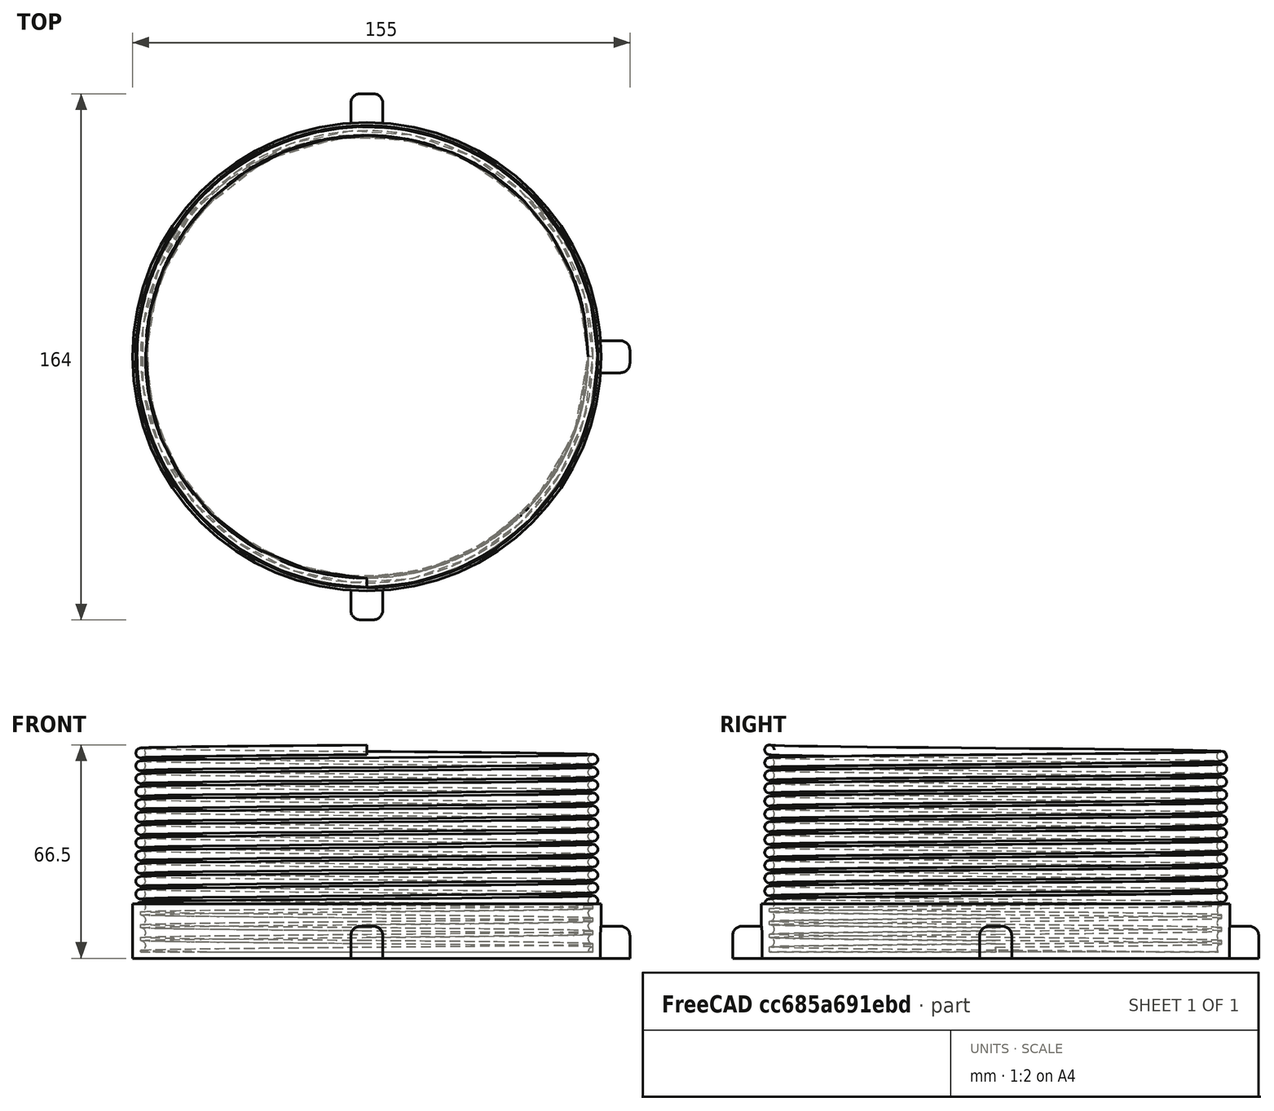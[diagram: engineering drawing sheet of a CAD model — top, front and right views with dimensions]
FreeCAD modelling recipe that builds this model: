
FCSTD DOCUMENT  (FreeCAD 0.19R24291 (Git))
Label: x_zem
License: All rights reserved
LicenseURL: http://en.wikipedia.org/wiki/All_rights_reserved
objects: Part::Box×3, Part::Fillet×3, Part::Helix×1, PartDesign::FeatureBase×1, Sketcher::SketchObject×1, Part::Sweep×1, Part::FeaturePython×1, Part::Cylinder×1, Part::MultiFuse×1, App::DocumentObjectGroup×1
note: 13 computed .brp shape members not serialized (recipe doc carries the construction recipe); baked Part::Feature solids carry a one-line shape summary decoded from their .brp

FEATURE [Part::Helix] Helix003  label="Helix_out002"
  Angle = 0
  AttacherType = Attacher::AttachEngine3D
  Height = 63
  LocalCoord = 0
  Pitch = 4
  Radius = 70.5
  Style = 1
FEATURE [PartDesign::FeatureBase] BaseFeature003
  BaseFeature = -> Helix003
FEATURE [Sketcher::SketchObject] Sketch003
  ExternalGeometry = -> [BaseFeature003]
  FullyConstrained = true
  MapMode = 5
  Placement = pos=(0,0,0) rot=(1,0,0;1.5708rad)
  Support = -> [XZ_Plane003]
  sketch-geometry (1):
    g0: Circle CenterX=70.5 CenterY=0 CenterZ=0 NormalX=0 NormalY=0 NormalZ=1 AngleXU=0 Radius=1.5
  constraints (2):
    c: Radius(g0) = 1.5
    c: Coincident(g0,g-3)
FEATURE [Part::Sweep] Sweep003  label="Sweep_out2 (bolo 70)"
  Frenet = true
  Placement = pos=(0,0,64) rot=(0,0,1;0rad)
  Sections = -> [Sketch003]
  Solid = true
  Spine = -> BaseFeature003 [Edge1,Edge2,Edge3,Edge4,Edge5,Edge6,Edge7,Edge8,Edge9,Edge10,Edge11,Edge12,Edge13,Edge14,Edge15,Edge16]
  Transition = 1
FEATURE [Part::FeaturePython] Tube001  label="Tube_vonkajsi_obal (70 dnu)"  # WARN: FeaturePython — macro-defined, semantics opaque (R4)
  AttacherType = Attacher::AttachEngine3D
  Height = 15
  InnerRadius = 70.5
  OuterRadius = 73
  Placement = pos=(0,0,64) rot=(0,0,1;0rad)
FEATURE [Part::Cylinder] Cylinder
  Angle = 360
  AttacherType = Attacher::AttachEngine3D
  Height = 2
  Placement = pos=(0,0,62) rot=(0,0,1;0rad)
  Radius = 73
FEATURE [Part::Box] Box  label="Cube"
  AttacherType = Attacher::AttachEngine3D
  Height = 10
  Length = 10
  Placement = pos=(-5,72,62) rot=(0,0,1;0rad)
  Width = 10
FEATURE [Part::Box] Box001  label="Cube001"
  AttacherType = Attacher::AttachEngine3D
  Height = 10
  Length = 10
  Placement = pos=(72,-5,62) rot=(0,0,1;0rad)
  Width = 10
FEATURE [Part::Box] Box002  label="Cube002"
  AttacherType = Attacher::AttachEngine3D
  Height = 10
  Length = 10
  Placement = pos=(-5,-82,62) rot=(0,0,1;0rad)
  Width = 10
FEATURE [Part::Fillet] Fillet
  Base = -> Box002
  Edges = 5 edges r=3: [Edge1,Edge2,Edge5,Edge6,Edge10]
FEATURE [Part::Fillet] Fillet001
  Base = -> Box001
  Edges = 5 edges r=3: [Edge5,Edge6,Edge7,Edge10,Edge12]
FEATURE [Part::Fillet] Fillet002
  Base = -> Box
  Edges = 5 edges r=3: [Edge2,Edge3,Edge6,Edge7,Edge12]
FEATURE [Part::MultiFuse] Fusion002
  Shapes = -> [Sweep003,Tube001,Cylinder,Fillet,Fillet001,Fillet002]
FEATURE [App::DocumentObjectGroup] Group  label="Cut_spodok"
  Group = -> [Fusion002,Helix003]
